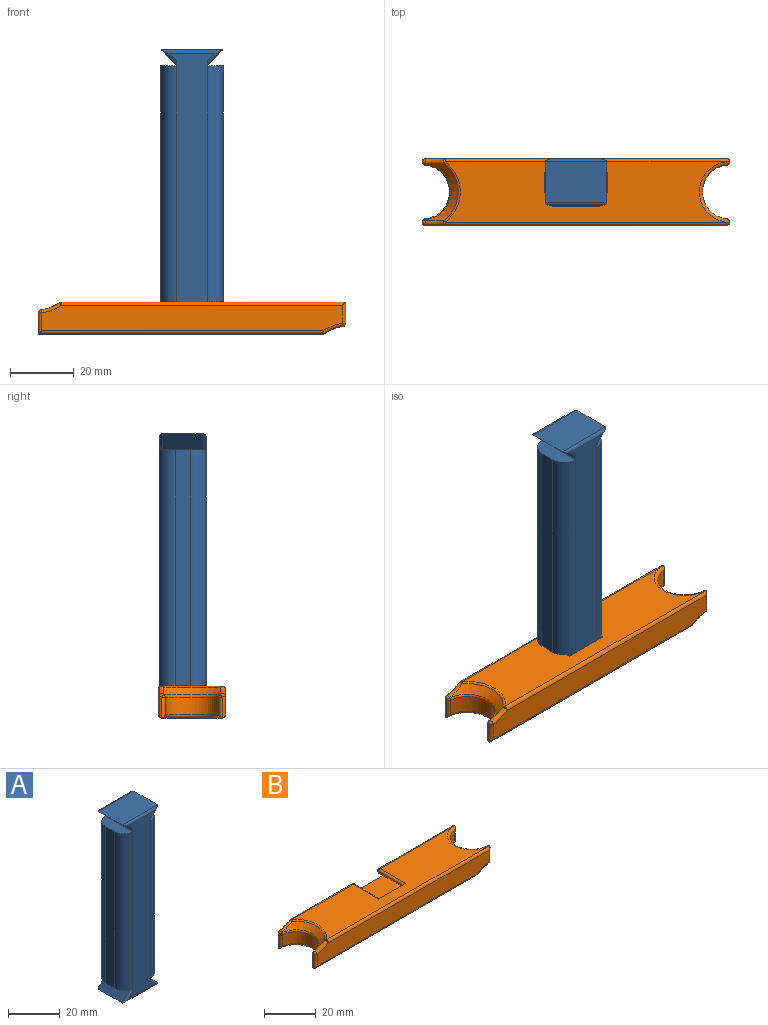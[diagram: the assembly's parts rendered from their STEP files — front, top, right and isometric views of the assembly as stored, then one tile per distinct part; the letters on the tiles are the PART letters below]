
ASSEMBLY  parts=2 mates=1
PART A: 34 faces, bbox 19.6x14.8x85.4 mm
  f0: plane 74x4.8mm, normal (-1,0,0), area 355.2mm2, adj f1,f15,f18,f20
  f1: plane 14.8x5mm, normal (0,0,-1), area 63.3mm2, adj f0,f2,f18,f20
  f2: plane 14.8x1.61mm, normal (-1,0,0), area 3.6mm2, adj f1,f3,f16,f17,f22,f28
  f3: plane 12.8x4.8mm, normal (-0.71,0,0.71), area 86.9mm2, adj f2,f4,f22,f28
  f4: plane 19.2x12.8mm, normal (0,0,-1), area 245.8mm2, adj f3,f5,f24,f30
  f5: plane 12.8x4.8mm, normal (0.71,0,0.71), area 86.9mm2, adj f4,f6,f23,f29
  f6: plane 14.8x1.61mm, normal (1,0,0), area 3.6mm2, adj f5,f7,f16,f17,f23,f29
  f7: plane 14.8x5mm, normal (0,0,-1), area 63.3mm2, adj f6,f8,f19,f21
  f8: plane 74x4.8mm, normal (1,0,0), area 355.2mm2, adj f7,f9,f19,f21
  f9: plane 14.8x5mm, normal (0,0,1), area 63.3mm2, adj f8,f10,f19,f21
  f10: plane 14.8x1.61mm, normal (1,0,0), area 3.6mm2, adj f9,f11,f16,f17,f25,f31
  f11: plane 12.8x4.8mm, normal (0.71,0,-0.71), area 86.9mm2, adj f10,f12,f25,f31
  f12: plane 19.2x12.8mm, normal (0,0,1), area 245.8mm2, adj f11,f13,f26,f32
  f13: plane 12.8x4.8mm, normal (-0.71,0,-0.71), area 86.9mm2, adj f12,f14,f27,f33
  f14: plane 14.8x1.61mm, normal (-1,0,0), area 3.6mm2, adj f13,f15,f16,f17,f27,f33
  f15: plane 14.8x5mm, normal (0,0,1), area 63.3mm2, adj f0,f14,f18,f20
  f16: plane 82x14.37mm, normal (0,-1,0), area 798.6mm2, adj f2,f6,f10,f14,f20,f21,f28,f29
  f17: plane 82x14.37mm, normal (0,1,0), area 798.6mm2, adj f2,f6,f10,f14,f18,f19,f22,f23
  f18: cylinder r=5mm len=74mm, axis (0,0,-1), area 581.2mm2, adj f0,f1,f15,f17
  f19: cylinder r=5mm len=74mm, axis (0,0,1), area 581.2mm2, adj f7,f8,f9,f17
  f20: cylinder r=5mm len=74mm, axis (0,0,1), area 581.2mm2, adj f0,f1,f15,f16
  f21: cylinder r=5mm len=74mm, axis (0,0,-1), area 581.2mm2, adj f7,f8,f9,f16
  f22: cylinder r=1mm len=5.51mm, axis (-0.71,0,-0.71), area 8.7mm2, adj f2,f3,f17,f24
  f23: cylinder r=1mm len=5.51mm, axis (-0.71,0,0.71), area 8.7mm2, adj f5,f6,f17,f24
  f24: cylinder r=1mm len=19.2mm, axis (1,0,0), area 27.4mm2, adj f4,f17,f22,f23
  f25: cylinder r=1mm len=5.51mm, axis (0.71,0,0.71), area 8.7mm2, adj f10,f11,f17,f26
  f26: cylinder r=1mm len=19.2mm, axis (-1,0,0), area 27.4mm2, adj f12,f17,f25,f27
  f27: cylinder r=1mm len=5.51mm, axis (0.71,0,-0.71), area 8.7mm2, adj f13,f14,f17,f26
  f28: cylinder r=1mm len=5.51mm, axis (0.71,0,0.71), area 8.7mm2, adj f2,f3,f16,f30
  f29: cylinder r=1mm len=5.51mm, axis (0.71,0,-0.71), area 8.7mm2, adj f5,f6,f16,f30
  f30: cylinder r=1mm len=19.2mm, axis (-1,0,0), area 27.4mm2, adj f4,f16,f28,f29
  f31: cylinder r=1mm len=5.51mm, axis (-0.71,0,-0.71), area 8.7mm2, adj f10,f11,f16,f32
  f32: cylinder r=1mm len=19.2mm, axis (1,0,0), area 27.4mm2, adj f12,f16,f31,f33
  f33: cylinder r=1mm len=5.51mm, axis (-0.71,0,0.71), area 8.7mm2, adj f13,f14,f16,f32
PART B: 61 faces, bbox 98.6x22.7x13.9 mm
  f0: plane 89.26x19mm, normal (0,0,1), area 1283.9mm2, adj f13,f16,f17,f20,f24,f31,f35,f55
  f1: plane 6.64x0.05mm, normal (-1,0,0), area 0.3mm2, adj f21,f28,f29,f50
  f2: cylinder r=8.5mm len=16.91mm, axis (0,0,-1), area 139.1mm2, adj f27,f28,f29,f54
  f3: plane 6.64x0.05mm, normal (-1,0,0), area 0.3mm2, adj f27,f28,f33,f58
  f4: plane 94.46x8.01mm, normal (0,-1,0), area 737.8mm2, adj f30,f31,f32,f33,f47,f59
  f5: plane 6.64x0.05mm, normal (1,0,0), area 0.3mm2, adj f30,f35,f36,f46
  f6: cylinder r=8.5mm len=16.91mm, axis (0,0,-1), area 139.1mm2, adj f34,f35,f36,f42
  f7: plane 6.64x0.05mm, normal (1,0,0), area 0.3mm2, adj f23,f34,f35,f38
  f8: plane 94.47x8.02mm, normal (0,1,0), area 662.5mm2, adj f11,f18,f20,f21,f22,f23,f24,f26
  f9: plane 89.26x19mm, normal (0,0,-1), area 1491.5mm2, adj f22,f28,f32,f43
  f10: plane 14x3.29mm, normal (-0.71,0,-0.71), area 65.2mm2, adj f11,f13,f16,f26
  f11: plane 23.25x15.42mm, normal (0,0,1), area 300.6mm2, adj f8,f10,f12,f13,f18,f26
  f12: plane 14x3.29mm, normal (0.71,0,-0.71), area 65.2mm2, adj f11,f13,f17,f18
  f13: plane 20x5mm, normal (0,1,0), area 77.5mm2, adj f0,f10,f11,f12,f16,f17
  f14: cone r=11.5mm half-angle=45deg, axis (0,0,-1), area 75.9mm2, adj f38,f39,f42,f43,f46,f47
  f15: cone r=11.5mm half-angle=45deg, axis (0,0,1), area 75.9mm2, adj f50,f51,f54,f55,f58,f59
  f16: cylinder r=1mm len=14mm, axis (0,-1,0), area 33mm2, adj f0,f10,f13,f25
  f17: cylinder r=1mm len=14mm, axis (0,-1,0), area 33mm2, adj f0,f12,f13,f19
  f18: cylinder r=1mm len=4.71mm, axis (-0.71,0,-0.71), area 8.1mm2, adj f8,f11,f12,f19
  f19: sphere r=1mm, area 2.4mm2, adj f17,f18,f20
  f20: cylinder r=1mm len=33.62mm, axis (1,0,0), area 52.8mm2, adj f0,f8,f19,f53
  f21: cylinder r=1mm len=6.64mm, axis (0,0,-1), area 9.6mm2, adj f1,f8,f22,f49
  f22: cylinder r=1mm len=89.26mm, axis (-1,0,0), area 139.4mm2, adj f8,f9,f21,f41
  f23: cylinder r=1mm len=6.64mm, axis (0,0,-1), area 9.6mm2, adj f7,f8,f24,f37
  f24: cylinder r=1mm len=40.81mm, axis (1,0,0), area 63.3mm2, adj f0,f8,f23,f25
  f25: sphere r=1mm, area 2.4mm2, adj f16,f24,f26
  f26: cylinder r=1mm len=4.71mm, axis (-0.71,0,0.71), area 8.1mm2, adj f8,f10,f11,f25
  f27: cylinder r=1mm len=6.58mm, axis (0,0,-1), area 8.9mm2, adj f2,f3,f28,f56
  f28: torus R=9.5mm, axis (0,0,1), area 42.7mm2, adj f1,f2,f3,f9,f27,f29
  f29: cylinder r=1mm len=6.58mm, axis (0,0,-1), area 8.9mm2, adj f1,f2,f28,f52
  f30: cylinder r=1mm len=6.64mm, axis (0,0,-1), area 9.6mm2, adj f4,f5,f31,f48
  f31: cylinder r=1mm len=89.26mm, axis (-1,0,0), area 139.4mm2, adj f0,f4,f30,f57
  f32: cylinder r=1mm len=89.26mm, axis (1,0,0), area 139.4mm2, adj f4,f9,f33,f45
  f33: cylinder r=1mm len=6.64mm, axis (0,0,-1), area 9.6mm2, adj f3,f4,f32,f60
  f34: cylinder r=1mm len=6.58mm, axis (0,0,-1), area 8.9mm2, adj f6,f7,f35,f40
  f35: torus R=9.5mm, axis (0,0,1), area 42.7mm2, adj f0,f5,f6,f7,f34,f36
  f36: cylinder r=1mm len=6.58mm, axis (0,0,-1), area 8.9mm2, adj f5,f6,f35,f44
  f37: sphere r=1mm, area 2mm2, adj f23,f38,f39
  f38: bspline ~0.93x0.89mm, area 0.1mm2, adj f7,f14,f37,f40
  f39: bspline ~9.16x4.63mm, area 14.4mm2, adj f8,f14,f37,f41
  f40: sphere r=1mm, area 0.9mm2, adj f34,f38,f42
  f41: sphere r=1mm, area 0.7mm2, adj f22,f39,f43
  f42: torus R=9.5mm, axis (0,0,1), area 19.8mm2, adj f6,f14,f40,f44
  f43: torus R=11.91mm, axis (0,0,1), area 16.7mm2, adj f9,f14,f41,f45
  f44: sphere r=1mm, area 0.9mm2, adj f36,f42,f46
  f45: sphere r=1mm, area 0.7mm2, adj f32,f43,f47
  f46: bspline ~0.93x0.89mm, area 0.1mm2, adj f5,f14,f44,f48
  f47: bspline ~8.85x5.15mm, area 14.4mm2, adj f4,f14,f45,f48
  f48: sphere r=1mm, area 2mm2, adj f30,f46,f47
  f49: sphere r=1mm, area 2mm2, adj f21,f50,f51
  f50: bspline ~0.93x0.89mm, area 0.1mm2, adj f1,f15,f49,f52
  f51: bspline ~9.16x4.63mm, area 14.4mm2, adj f8,f15,f49,f53
  f52: sphere r=1mm, area 0.9mm2, adj f29,f50,f54
  f53: sphere r=1mm, area 0.7mm2, adj f20,f51,f55
  f54: torus R=9.5mm, axis (0,0,-1), area 19.8mm2, adj f2,f15,f52,f56
  f55: torus R=11.91mm, axis (0,0,1), area 16.7mm2, adj f0,f15,f53,f57
  f56: sphere r=1mm, area 0.9mm2, adj f27,f54,f58
  f57: sphere r=1mm, area 0.7mm2, adj f31,f55,f59
  f58: bspline ~0.93x0.89mm, area 0.1mm2, adj f3,f15,f56,f60
  f59: bspline ~8.85x5.15mm, area 14.4mm2, adj f4,f15,f57,f60
  f60: sphere r=1mm, area 2mm2, adj f33,f58,f59
PLACE A t=(-3.76,25.68,-14.09)mm
PLACE B t=(-3.76,15.38,-14.09)mm
MATE parallel A.f4 <-> B.f11  axis (0,0,-1) through (-3.76,18.28,-8.89)mm
